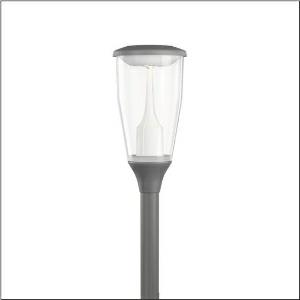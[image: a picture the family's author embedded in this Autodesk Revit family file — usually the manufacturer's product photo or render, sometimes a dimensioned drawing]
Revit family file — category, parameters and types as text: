
# Revit family: dl_11_iq___st1_2a_5xa5575af14hp00022_5e00
name_source: partatom
category: Lighting Fixtures
units: mm (PartAtom-declared; Revit-internal decimal feet)

## family parameters
Cut with Voids When Loaded = No
Host = Face
Light Source = No
Part Type = Normal
Room Calculation Point = No
Round Connector Dimension = Use Diameter
Shared = No

## types (1)
- --- (1 x LED, 4000 lm, 33.6 W, 2200K)
    Apparent Load = 34 VA
    CIE Flux Codes = 23 60 93 95 100
    Color Rendering = 70
    Color Temperature = 2200K
    Default Elevation = 1800 mm
    Description = DL 11 iQ, mast luminaire, Module 540 iQ-SR, primary light control with 3 zone facetted reflector, of plastic, silver coated, highly specular, structured, primary optical cover: cover, of PMMA, transparent, light distribution: ST1.2a, light emission: direct distribution, primary light characteristic: asymmetric, installation type: post-top, LED, High Power LED, rated luminous flux: 4.000lm, luminous efficacy: 119lm/W, light colour: 722, colour temperature: 2200K, control gear: iQ Street-Remote, control: Street-Remote, Auto-Match, Temp-Guard, Lumen-Switch, Night-Set, Smart-Wire, Light-Fading, Desk-Remote (wireless, voltage-free reading and setting of iQ features in the workshop via application-optimized NFC function/RFID function), optimised constant luminous flux control (CLO 2.0), mains connection: 220..240V, AC, 50/60Hz, connection cable pre-assembled, cable length: 5,5m, start of lifetime: 34W, end of service life: 36W, reduction: 15W, luminaire housing, upper part, of diecast aluminium, coated, Siteco® metallic grey (DB 702S), spigot size: 76mm (post-top), mounting height: 3..5m, post-top mast mounting element, of diecast aluminium, coated, Siteco® metallic grey (DB 702S), Module 540 iQ-SR, traffic white (RAL 9016), equipment: Power, protection rating (complete): IP66, insulation class (complete): insulation class II (safety insulation), certification: CE, ENEC, ENEC+, VDE, impact resistance: IK07, packaging unit: 1 piece

Light Distribution: ST1.2a
    Height = 665 mm
    Lamp = 1 x LED
    Lamp Light Flux = 4000 lm
    Lamp Power = 33.6 W
    Lamp count = 1
    Length = 334 mm
    Luminous efficacy = 119 lm/W
    Manufacturer = Siteco
    ModVariant = No
    Model = 5XA5575AF14HP00022
    Number of Poles = 1
    OnlyDefault = Yes
    Power Factor = 1
    Product Name = DL 11 iQ | ST1.2a
    Product group = mast luminaire | pylon top
    ProductGroupID = 6100
    Protection Class = Protection class II
    Protection Degree = IP 66
    RLX_Detail_Level = 1
    RLX_Emergency_Light_Flux = 0 lm
    RLX_Emergency_Type = 0
    RLX_Emergency_Type_DB = No
    RlxData = <blob elided: 154209 chars, md5=021e0043>
    Socket = socket
    Standby Power = 0 W
    System Light Flux = 4000 lm
    System Power = 34 W
    Type Comments = factory setting: luminous flux: 100 % | dim-lin: 254 | 695 mA
    Type Image = l_1258354.jpg
    URL = http://relux.com
    VarID = @adj_033588
    Voltage = 0 V
    Weight = 0.00 kg
    Width = 0 mm  [stored 0 ft]

note: [stored X ft] marks values corroborated as IEEE doubles in the binary element streams (Revit-internal decimal feet)

## geometry (parser evidence)
native form markers: Blend x4, Sweep x10
no freeform markers — native parametric forms only
